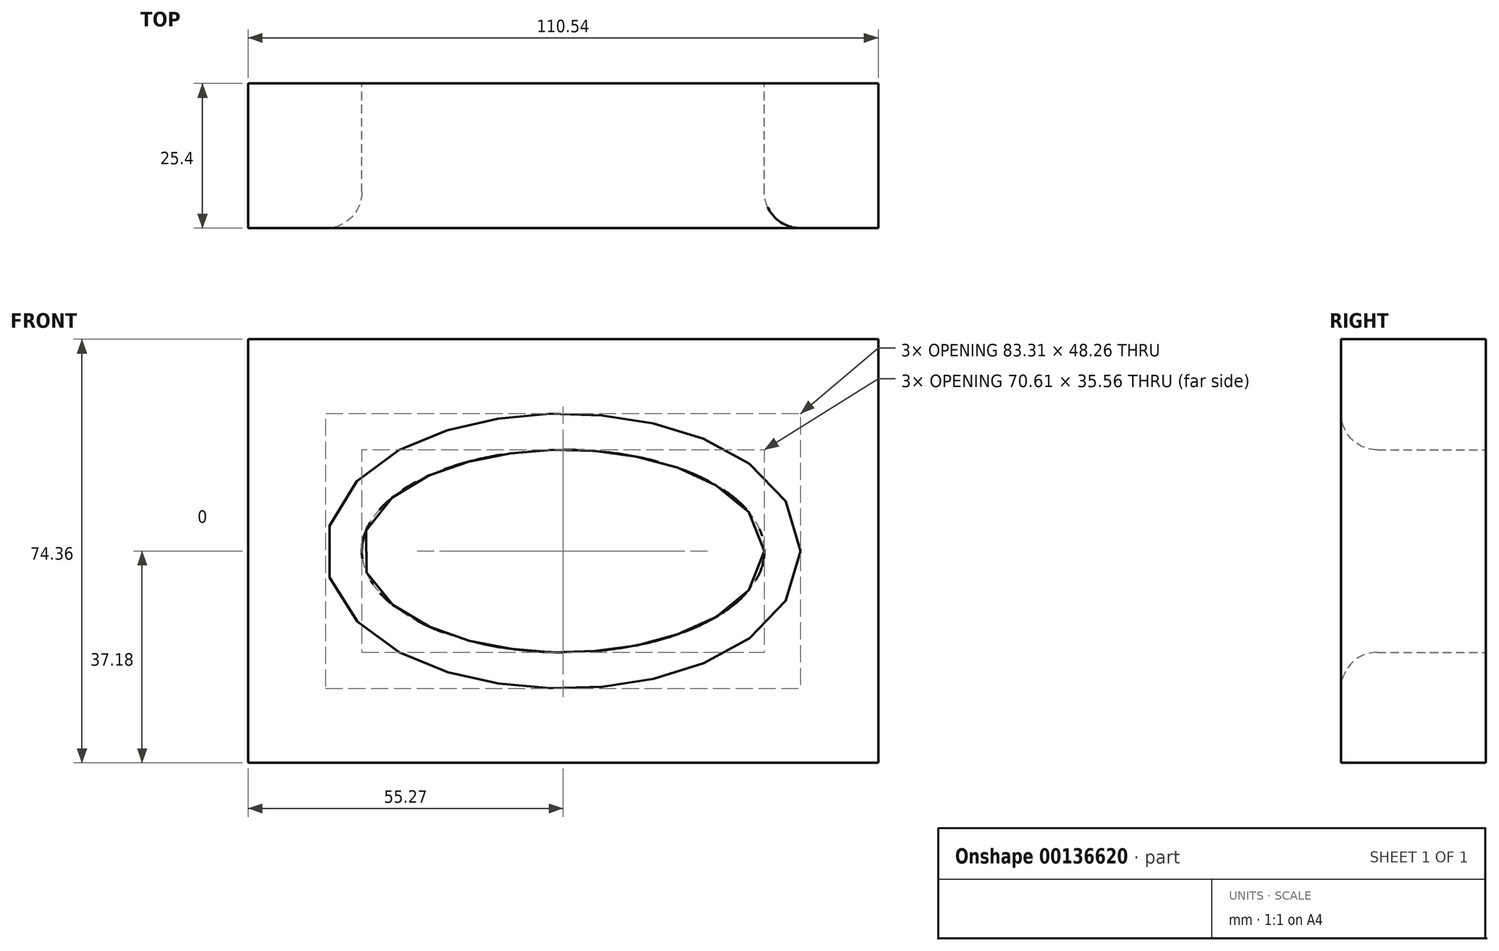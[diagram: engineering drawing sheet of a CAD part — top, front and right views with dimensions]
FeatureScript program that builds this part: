
annotation { "Feature Type Name" : "Feature", "Feature Type Description" : "" }
export const myFeature = defineFeature(function(context is Context, id is Id, definition is map)
    precondition{}
    {
        {
            var Q0;
            Q0=qCreatedBy(makeId("Front.planeOp"),FACE);
            var sketch = newSketch(context, id + "F0", { "sketchPlane" : qUnion([Q0])});
            skLineSegment(sketch, "E0.bottom", {"start": v(55.27, -37.18) * mm, "end": v(-55.27, -37.18) * mm});
            skLineSegment(sketch, "E0.top", {"start": v(55.27, 37.18) * mm, "end": v(-55.27, 37.18) * mm});
            skLineSegment(sketch, "E0.left", {"start": v(55.27, -37.18) * mm, "end": v(55.27, 37.18) * mm});
            skLineSegment(sketch, "E0.right", {"start": v(-55.27, -37.18) * mm, "end": v(-55.27, 37.18) * mm});
            skPoint(sketch, "E0.middle", {"position": v(0, 0) * mm});
            skEllipse(sketch, "E1", {"center": v(0, 0) * mm, "majorRadius": 35.3 * mm, "minorRadius": 17.78 * mm, "majorAxis": v(1, 0)});
            skSolve(sketch);
        }
        {
            var Q0;
            Q0=makeQuery(id+"F0.imprint","IMPRINT",FACE,{"disambiguationData":[TD([[makeQuery(id+"F0.imprint","IMPRINT",EDGE,{"derivedFrom":sQuery(id+"F0.wireOp",EDGE,"E0.bottom")}),-1.0]])]});
            extrude(context, id + "F1", {"entities" : qUnion([Q0]), "depth" : 25.4 * mm});
        }
        {
            var Q0;
            Q0=makeQuery(id+"F1.opExtrude","CAP_EDGE",EDGE,{"disambiguationData":[OSD([sQuery(id+"F0.wireOp",EDGE,"E1")])],"isStart":false});
            fillet(context, id + "F2", {"entities" : qUnion([Q0]), "radius" : 6.35 * mm, "tangentPropagation" : true, "allowEdgeOverflow" : false});
        }
    });
